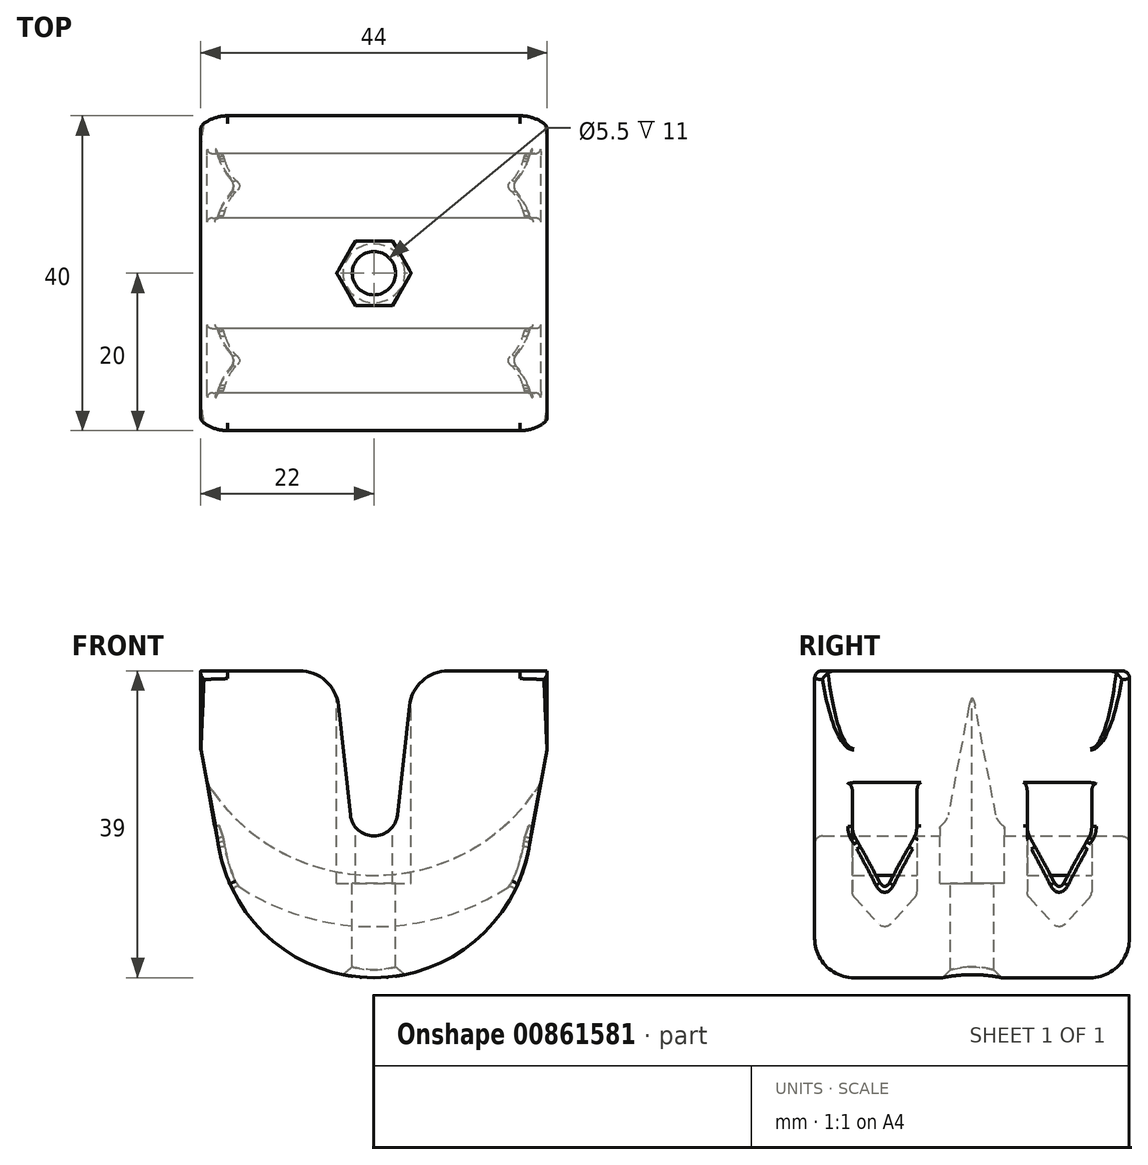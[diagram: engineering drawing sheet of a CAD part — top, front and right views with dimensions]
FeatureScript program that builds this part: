
annotation { "Feature Type Name" : "Feature", "Feature Type Description" : "" }
export const myFeature = defineFeature(function(context is Context, id is Id, definition is map)
    precondition{}
    {
        {
            var Q0;
            Q0=qCreatedBy(makeId("Front.planeOp"),FACE);
            var sketch = newSketch(context, id + "F0", { "sketchPlane" : qUnion([Q0])});
            skArc(sketch, "E0", {"start": v(2.98, -0.33) * mm, "mid": v(2, -2.23) * mm, "end": v(0, -3) * mm});
            skLineSegment(sketch, "E1", {"start": v(2.98, -0.33) * mm, "end": v(5, 18) * mm});
            skLineSegment(sketch, "E2", {"start": v(5, 18) * mm, "end": v(22, 18) * mm});
            skLineSegment(sketch, "E3", {"start": v(22, 18) * mm, "end": v(22, 8) * mm});
            skLineSegment(sketch, "E4", {"start": v(22, 8) * mm, "end": v(19.67, -4.63) * mm});
            skArc(sketch, "E5", {"start": v(19.67, -4.63) * mm, "mid": v(12.8, -16.37) * mm, "end": v(0, -21) * mm});
            skArc(sketch, "E6.MirrorCS", {"start": v(-2.98, -0.33) * mm, "mid": v(-2, -2.23) * mm, "end": v(0, -3) * mm});
            skLineSegment(sketch, "E7.MirrorCS", {"start": v(-5, 18) * mm, "end": v(-22, 18) * mm});
            skLineSegment(sketch, "E8.MirrorCS", {"start": v(-22, 8) * mm, "end": v(-19.67, -4.63) * mm});
            skLineSegment(sketch, "E9.MirrorCS", {"start": v(-2.98, -0.33) * mm, "end": v(-5, 18) * mm});
            skLineSegment(sketch, "E10.MirrorCS", {"start": v(-22, 18) * mm, "end": v(-22, 8) * mm});
            skArc(sketch, "E11.MirrorCS", {"start": v(-19.67, -4.63) * mm, "mid": v(-12.8, -16.37) * mm, "end": v(0, -21) * mm});
            skSolve(sketch);
        }
        {
            var Q0;
            Q0 = qSketchRegion(id + "F0", true);
            extrude(context, id + "F1", {"entities" : qUnion([Q0]), "depth" : 20 * mm, "offsetDistance" : 25 * mm, "hasSecondDirection" : true, "secondDirectionOppositeDirection" : true, "secondDirectionDepth" : 20 * mm});
        }
        {
            var Q0;
            Q0=makeQuery(id+"F1.opExtrude","SWEPT_FACE",FACE,{"disambiguationData":[OSD([sQuery(id+"F0.wireOp",EDGE,"E2")])]});
            var sketch = newSketch(context, id + "F2", { "sketchPlane" : qUnion([Q0])});
            skCircle(sketch, "E12.cCircle", {"center": v(0, 0) * mm, "radius": 4.1 * mm, "construction": true});
            skLineSegment(sketch, "E12.0", {"start": v(2.37, 4.1) * mm, "end": v(4.73, 0) * mm});
            skLineSegment(sketch, "E12.1", {"start": v(4.73, 0) * mm, "end": v(2.37, -4.1) * mm});
            skLineSegment(sketch, "E12.2", {"start": v(2.37, -4.1) * mm, "end": v(-2.37, -4.1) * mm});
            skLineSegment(sketch, "E12.3", {"start": v(-2.37, -4.1) * mm, "end": v(-4.73, 0) * mm});
            skLineSegment(sketch, "E12.4", {"start": v(-4.73, 0) * mm, "end": v(-2.37, 4.1) * mm});
            skLineSegment(sketch, "E12.5", {"start": v(-2.37, 4.1) * mm, "end": v(2.37, 4.1) * mm});
            skPoint(sketch, "E12.0.midPoint", {"position": v(3.55, 2.05) * mm});
            skSolve(sketch);
        }
        {
            var Q0;
            Q0 = qSketchRegion(id + "F2", true);
            extrude(context, id + "F3", {"entities" : qUnion([Q0]), "operationType" : NewBodyOperationType.REMOVE, "oppositeDirection" : true, "depth" : 27 * mm, "offsetDistance" : 25 * mm});
        }
        {
            var Q0;
            Q0=makeQuery(id+"F1.opExtrude","SWEPT_EDGE",EDGE,{"disambiguationData":[OSD([sQuery(id+"F0.wireOp",EDGE,"E1"),sQuery(id+"F0.wireOp",EDGE,"E2")])]});
            var Q1;
            Q1=makeQuery(id+"F1.opExtrude","SWEPT_EDGE",EDGE,{"disambiguationData":[OSD([sQuery(id+"F0.wireOp",EDGE,"E7.MirrorCS"),sQuery(id+"F0.wireOp",EDGE,"E9.MirrorCS")])]});
            fillet(context, id + "F4", {"entities" : qUnion([Q0, Q1]), "radius" : 5 * mm, "tangentPropagation" : true, "allowEdgeOverflow" : false});
        }
        {
            var Q0;
            Q0=makeQuery(id+"F3.boolean.opBoolean","COPY",FACE,{"derivedFrom":makeQuery(id+"F3.opExtrude","CAP_FACE",FACE,{"disambiguationData":[OSD([sQuery(id+"F2.wireOp",EDGE,"E12.0"),sQuery(id+"F2.wireOp",EDGE,"E12.1"),sQuery(id+"F2.wireOp",EDGE,"E12.2"),sQuery(id+"F2.wireOp",EDGE,"E12.3"),sQuery(id+"F2.wireOp",EDGE,"E12.4"),sQuery(id+"F2.wireOp",EDGE,"E12.5")])],"isStart":false})});
            var sketch = newSketch(context, id + "F5", { "sketchPlane" : qUnion([Q0])});
            skCircle(sketch, "E13", {"center": v(0, 0) * mm, "radius": 2.75 * mm});
            skSolve(sketch);
        }
        {
            var Q0;
            Q0 = qSketchRegion(id + "F5", true);
            extrude(context, id + "F6", {"entities" : qUnion([Q0]), "operationType" : NewBodyOperationType.REMOVE, "endBound" : BoundingType.THROUGH_ALL, "oppositeDirection" : true, "depth" : 25 * mm, "offsetDistance" : 25 * mm});
        }
        {
            var Q0;
            Q0=qCreatedBy(makeId("Right.planeOp"),FACE);
            var sketch = newSketch(context, id + "F7", { "sketchPlane" : qUnion([Q0])});
            skLineSegment(sketch, "E14.top", {"start": v(-15.2, -8) * mm, "end": v(-7, -8) * mm});
            skLineSegment(sketch, "E14.left", {"start": v(-15.2, -10.11) * mm, "end": v(-15.2, -8) * mm});
            skLineSegment(sketch, "E14.right", {"start": v(-7, -10.11) * mm, "end": v(-7, -8) * mm});
            skLineSegment(sketch, "E15.MirrorCS", {"start": v(7, -10.12) * mm, "end": v(7, -8) * mm});
            skLineSegment(sketch, "E16.MirrorCS", {"start": v(15.2, -10.1) * mm, "end": v(15.2, -8) * mm});
            skLineSegment(sketch, "E17.MirrorCS", {"start": v(15.2, -8) * mm, "end": v(7, -8) * mm});
            skLineSegment(sketch, "E18", {"start": v(-20, 17) * mm, "end": v(20, 17) * mm});
            skLineSegment(sketch, "E19", {"start": v(-14.94, -10.79) * mm, "end": v(-11.84, -14.19) * mm});
            skLineSegment(sketch, "E20", {"start": v(-10.36, -14.19) * mm, "end": v(-7.26, -10.79) * mm});
            skLineSegment(sketch, "E21", {"start": v(7.26, -10.79) * mm, "end": v(10.32, -14.18) * mm});
            skLineSegment(sketch, "E22", {"start": v(11.8, -14.2) * mm, "end": v(14.94, -10.79) * mm});
            skPoint(sketch, "E23.visualSharp", {"position": v(-15.2, -10.5) * mm});
            skArc(sketch, "E23.filletArc", {"start": v(-15.2, -10.11) * mm, "mid": v(-15.13, -10.47) * mm, "end": v(-14.94, -10.79) * mm});
            skPoint(sketch, "E24.visualSharp", {"position": v(-7, -10.5) * mm});
            skArc(sketch, "E24.filletArc", {"start": v(-7.26, -10.79) * mm, "mid": v(-7.07, -10.47) * mm, "end": v(-7, -10.11) * mm});
            skPoint(sketch, "E25.visualSharp", {"position": v(7, -10.5) * mm});
            skArc(sketch, "E25.filletArc", {"start": v(7, -10.12) * mm, "mid": v(7.07, -10.47) * mm, "end": v(7.26, -10.79) * mm});
            skPoint(sketch, "E26.visualSharp", {"position": v(15.2, -10.5) * mm});
            skArc(sketch, "E26.filletArc", {"start": v(14.94, -10.79) * mm, "mid": v(15.13, -10.47) * mm, "end": v(15.2, -10.1) * mm});
            skPoint(sketch, "E27.visualSharp", {"position": v(-11.1, -15) * mm});
            skArc(sketch, "E27.filletArc", {"start": v(-11.84, -14.19) * mm, "mid": v(-11.1, -14.52) * mm, "end": v(-10.36, -14.19) * mm});
            skPoint(sketch, "E28.visualSharp", {"position": v(11.05, -15) * mm});
            skArc(sketch, "E28.filletArc", {"start": v(10.32, -14.18) * mm, "mid": v(11.06, -14.52) * mm, "end": v(11.8, -14.2) * mm});
            skSolve(sketch);
        }
        {
            var Q0;
            Q0 = qSketchRegion(id + "F7", true);
            var Q1;
            Q1=sQuery(id+"F7.wireOp",EDGE,"E18");
            revolve(context, id + "F8", {"operationType" : NewBodyOperationType.REMOVE, "surfaceOperationType" : NewSurfaceOperationType.NEW, "entities" : qUnion([Q0]), "axis" : qUnion([Q1]), "revolveType" : RevolveType.FULL, "oppositeDirection" : true});
        }
        {
            var Q0;
            Q0=makeQuery(id+"F1.opExtrude","CAP_EDGE",EDGE,{"disambiguationData":[OSD([sQuery(id+"F0.wireOp",EDGE,"E4")])],"isStart":false});
            var Q1;
            Q1=makeQuery(id+"F1.opExtrude","CAP_EDGE",EDGE,{"disambiguationData":[OSD([sQuery(id+"F0.wireOp",EDGE,"E5"),sQuery(id+"F0.wireOp",EDGE,"E11.MirrorCS")])],"isStart":true});
            fillet(context, id + "F9", {"entities" : qUnion([Q0, Q1]), "radius" : 5 * mm, "tangentPropagation" : true, "allowEdgeOverflow" : false});
        }
        {
            var Q0;
            Q0=makeQuery(id+"F8.boolean.opBoolean","INTERSECT",EDGE,{"derivedFrom":[makeQuery(id+"F1.opExtrude","SWEPT_FACE",FACE,{"disambiguationData":[OSD([sQuery(id+"F0.wireOp",EDGE,"E8.MirrorCS")])]}),makeQuery(id+"F8.opRevolve","SWEPT_FACE",FACE,{"disambiguationData":[OSD([sQuery(id+"F7.wireOp",EDGE,"E19")])]})]});
            var Q1;
            Q1=makeQuery(id+"F8.boolean.opBoolean","INTERSECT",EDGE,{"derivedFrom":[makeQuery(id+"F1.opExtrude","SWEPT_FACE",FACE,{"disambiguationData":[OSD([sQuery(id+"F0.wireOp",EDGE,"E8.MirrorCS")])]}),makeQuery(id+"F8.opRevolve","SWEPT_FACE",FACE,{"disambiguationData":[OSD([sQuery(id+"F7.wireOp",EDGE,"E20")])]})]});
            var Q2;
            Q2=makeQuery(id+"F9.opFillet","BLEND_EDGE",EDGE,{"blendedFrom":[makeQuery(id+"F1.opExtrude","CAP_EDGE",EDGE,{"disambiguationData":[OSD([sQuery(id+"F0.wireOp",EDGE,"E8.MirrorCS")])],"isStart":false}),makeQuery(id+"F8.boolean.opBoolean","COPY",FACE,{"derivedFrom":makeQuery(id+"F8.opRevolve","SWEPT_FACE",FACE,{"disambiguationData":[OSD([sQuery(id+"F7.wireOp",EDGE,"E19")])]})})],"blendedInto":[makeQuery(id+"F8.boolean.opBoolean","COPY",FACE,{"derivedFrom":makeQuery(id+"F8.opRevolve","SWEPT_FACE",FACE,{"disambiguationData":[OSD([sQuery(id+"F7.wireOp",EDGE,"E19")])]})})]});
            var Q3;
            Q3=makeQuery(id+"F8.boolean.opBoolean","INTERSECT",EDGE,{"derivedFrom":[makeQuery(id+"F1.opExtrude","SWEPT_FACE",FACE,{"disambiguationData":[OSD([sQuery(id+"F0.wireOp",EDGE,"E8.MirrorCS")])]}),makeQuery(id+"F8.opRevolve","SWEPT_FACE",FACE,{"disambiguationData":[OSD([sQuery(id+"F7.wireOp",EDGE,"E27.filletArc")])]})]});
            var Q4;
            Q4=makeQuery(id+"F8.boolean.opBoolean","INTERSECT",EDGE,{"derivedFrom":[makeQuery(id+"F1.opExtrude","SWEPT_FACE",FACE,{"disambiguationData":[OSD([sQuery(id+"F0.wireOp",EDGE,"E8.MirrorCS")])]}),makeQuery(id+"F8.opRevolve","SWEPT_FACE",FACE,{"disambiguationData":[OSD([sQuery(id+"F7.wireOp",EDGE,"E21")])]})]});
            var Q5;
            Q5=makeQuery(id+"F8.boolean.opBoolean","INTERSECT",EDGE,{"derivedFrom":[makeQuery(id+"F1.opExtrude","SWEPT_FACE",FACE,{"disambiguationData":[OSD([sQuery(id+"F0.wireOp",EDGE,"E4")])]}),makeQuery(id+"F8.opRevolve","SWEPT_FACE",FACE,{"disambiguationData":[OSD([sQuery(id+"F7.wireOp",EDGE,"E22")])]})]});
            var Q6;
            Q6=makeQuery(id+"F8.boolean.opBoolean","INTERSECT",EDGE,{"derivedFrom":[makeQuery(id+"F1.opExtrude","SWEPT_FACE",FACE,{"disambiguationData":[OSD([sQuery(id+"F0.wireOp",EDGE,"E4")])]}),makeQuery(id+"F8.opRevolve","SWEPT_FACE",FACE,{"disambiguationData":[OSD([sQuery(id+"F7.wireOp",EDGE,"E20")])]})]});
            fillet(context, id + "F10", {"entities" : qUnion([Q0, Q1, Q2, Q3, Q4, Q5, Q6]), "radius" : 0.5 * mm, "tangentPropagation" : true, "allowEdgeOverflow" : false});
        }
        {
            var Q0;
            Q0=makeQuery(id+"F6.boolean.opBoolean","INTERSECT",EDGE,{"derivedFrom":[makeQuery(id+"F1.opExtrude","SWEPT_FACE",FACE,{"disambiguationData":[OSD([sQuery(id+"F0.wireOp",EDGE,"E5"),sQuery(id+"F0.wireOp",EDGE,"E11.MirrorCS")])]}),makeQuery(id+"F6.opExtrude","SWEPT_FACE",FACE,{"disambiguationData":[OSD([sQuery(id+"F5.wireOp",EDGE,"E13")])]})]});
            chamfer(context, id + "F11", {"entities" : qUnion([Q0]), "width" : 1 * mm, "tangentPropagation" : true});
        }
        {
            var Q0;
            Q0=makeQuery(id+"F9.opFillet","BLEND_EDGE",EDGE,{"blendedFrom":[makeQuery(id+"F1.opExtrude","CAP_EDGE",EDGE,{"disambiguationData":[OSD([sQuery(id+"F0.wireOp",EDGE,"E4")])],"isStart":false}),makeQuery(id+"F1.opExtrude","SWEPT_FACE",FACE,{"disambiguationData":[OSD([sQuery(id+"F0.wireOp",EDGE,"E2")])]})],"blendedInto":[makeQuery(id+"F1.opExtrude","SWEPT_FACE",FACE,{"disambiguationData":[OSD([sQuery(id+"F0.wireOp",EDGE,"E2")])]})]});
            var Q1;
            Q1=makeQuery(id+"F9.opFillet","BLEND_EDGE",EDGE,{"blendedFrom":[makeQuery(id+"F1.opExtrude","CAP_EDGE",EDGE,{"disambiguationData":[OSD([sQuery(id+"F0.wireOp",EDGE,"E4")])],"isStart":true}),makeQuery(id+"F1.opExtrude","SWEPT_FACE",FACE,{"disambiguationData":[OSD([sQuery(id+"F0.wireOp",EDGE,"E3")])]})],"blendedInto":[makeQuery(id+"F1.opExtrude","SWEPT_FACE",FACE,{"disambiguationData":[OSD([sQuery(id+"F0.wireOp",EDGE,"E3")])]})]});
            var Q2;
            Q2=makeQuery(id+"F1.opExtrude","SWEPT_EDGE",EDGE,{"disambiguationData":[OSD([sQuery(id+"F0.wireOp",EDGE,"E3"),sQuery(id+"F0.wireOp",EDGE,"E4")])]});
            var Q3;
            Q3=makeQuery(id+"F9.opFillet","BLEND_EDGE",EDGE,{"blendedFrom":[makeQuery(id+"F1.opExtrude","CAP_EDGE",EDGE,{"disambiguationData":[OSD([sQuery(id+"F0.wireOp",EDGE,"E4")])],"isStart":false}),makeQuery(id+"F1.opExtrude","SWEPT_FACE",FACE,{"disambiguationData":[OSD([sQuery(id+"F0.wireOp",EDGE,"E3")])]})],"blendedInto":[makeQuery(id+"F1.opExtrude","SWEPT_FACE",FACE,{"disambiguationData":[OSD([sQuery(id+"F0.wireOp",EDGE,"E3")])]})]});
            var Q4;
            Q4=makeQuery(id+"F9.opFillet","BLEND_EDGE",EDGE,{"blendedFrom":[makeQuery(id+"F1.opExtrude","CAP_EDGE",EDGE,{"disambiguationData":[OSD([sQuery(id+"F0.wireOp",EDGE,"E8.MirrorCS")])],"isStart":false}),makeQuery(id+"F1.opExtrude","SWEPT_FACE",FACE,{"disambiguationData":[OSD([sQuery(id+"F0.wireOp",EDGE,"E10.MirrorCS")])]})],"blendedInto":[makeQuery(id+"F1.opExtrude","SWEPT_FACE",FACE,{"disambiguationData":[OSD([sQuery(id+"F0.wireOp",EDGE,"E10.MirrorCS")])]})]});
            var Q5;
            Q5=makeQuery(id+"F1.opExtrude","SWEPT_EDGE",EDGE,{"disambiguationData":[OSD([sQuery(id+"F0.wireOp",EDGE,"E8.MirrorCS"),sQuery(id+"F0.wireOp",EDGE,"E10.MirrorCS")])]});
            var Q6;
            Q6=makeQuery(id+"F9.opFillet","BLEND_EDGE",EDGE,{"blendedFrom":[makeQuery(id+"F1.opExtrude","CAP_EDGE",EDGE,{"disambiguationData":[OSD([sQuery(id+"F0.wireOp",EDGE,"E8.MirrorCS")])],"isStart":true}),makeQuery(id+"F1.opExtrude","SWEPT_FACE",FACE,{"disambiguationData":[OSD([sQuery(id+"F0.wireOp",EDGE,"E10.MirrorCS")])]})],"blendedInto":[makeQuery(id+"F1.opExtrude","SWEPT_FACE",FACE,{"disambiguationData":[OSD([sQuery(id+"F0.wireOp",EDGE,"E10.MirrorCS")])]})]});
            var Q7;
            Q7=makeQuery(id+"F1.opExtrude","CAP_EDGE",EDGE,{"disambiguationData":[OSD([sQuery(id+"F0.wireOp",EDGE,"E9.MirrorCS")])],"isStart":true});
            var Q8;
            Q8=makeQuery(id+"F1.opExtrude","CAP_EDGE",EDGE,{"disambiguationData":[OSD([sQuery(id+"F0.wireOp",EDGE,"E0"),sQuery(id+"F0.wireOp",EDGE,"E6.MirrorCS")])],"isStart":true});
            var Q9;
            Q9=makeQuery(id+"F1.opExtrude","CAP_EDGE",EDGE,{"disambiguationData":[OSD([sQuery(id+"F0.wireOp",EDGE,"E1")])],"isStart":true});
            var Q10;
            Q10=makeQuery(id+"F1.opExtrude","CAP_EDGE",EDGE,{"disambiguationData":[OSD([sQuery(id+"F0.wireOp",EDGE,"E0"),sQuery(id+"F0.wireOp",EDGE,"E6.MirrorCS")])],"isStart":false});
            var Q11;
            Q11=makeQuery(id+"F1.opExtrude","CAP_EDGE",EDGE,{"disambiguationData":[OSD([sQuery(id+"F0.wireOp",EDGE,"E9.MirrorCS")])],"isStart":false});
            var Q12;
            Q12=makeQuery(id+"F1.opExtrude","CAP_EDGE",EDGE,{"disambiguationData":[OSD([sQuery(id+"F0.wireOp",EDGE,"E1")])],"isStart":false});
            fillet(context, id + "F12", {"entities" : qUnion([Q0, Q1, Q2, Q3, Q4, Q5, Q6, Q7, Q8, Q9, Q10, Q11, Q12]), "radius" : 1 * mm, "tangentPropagation" : true, "allowEdgeOverflow" : false});
        }
    });
